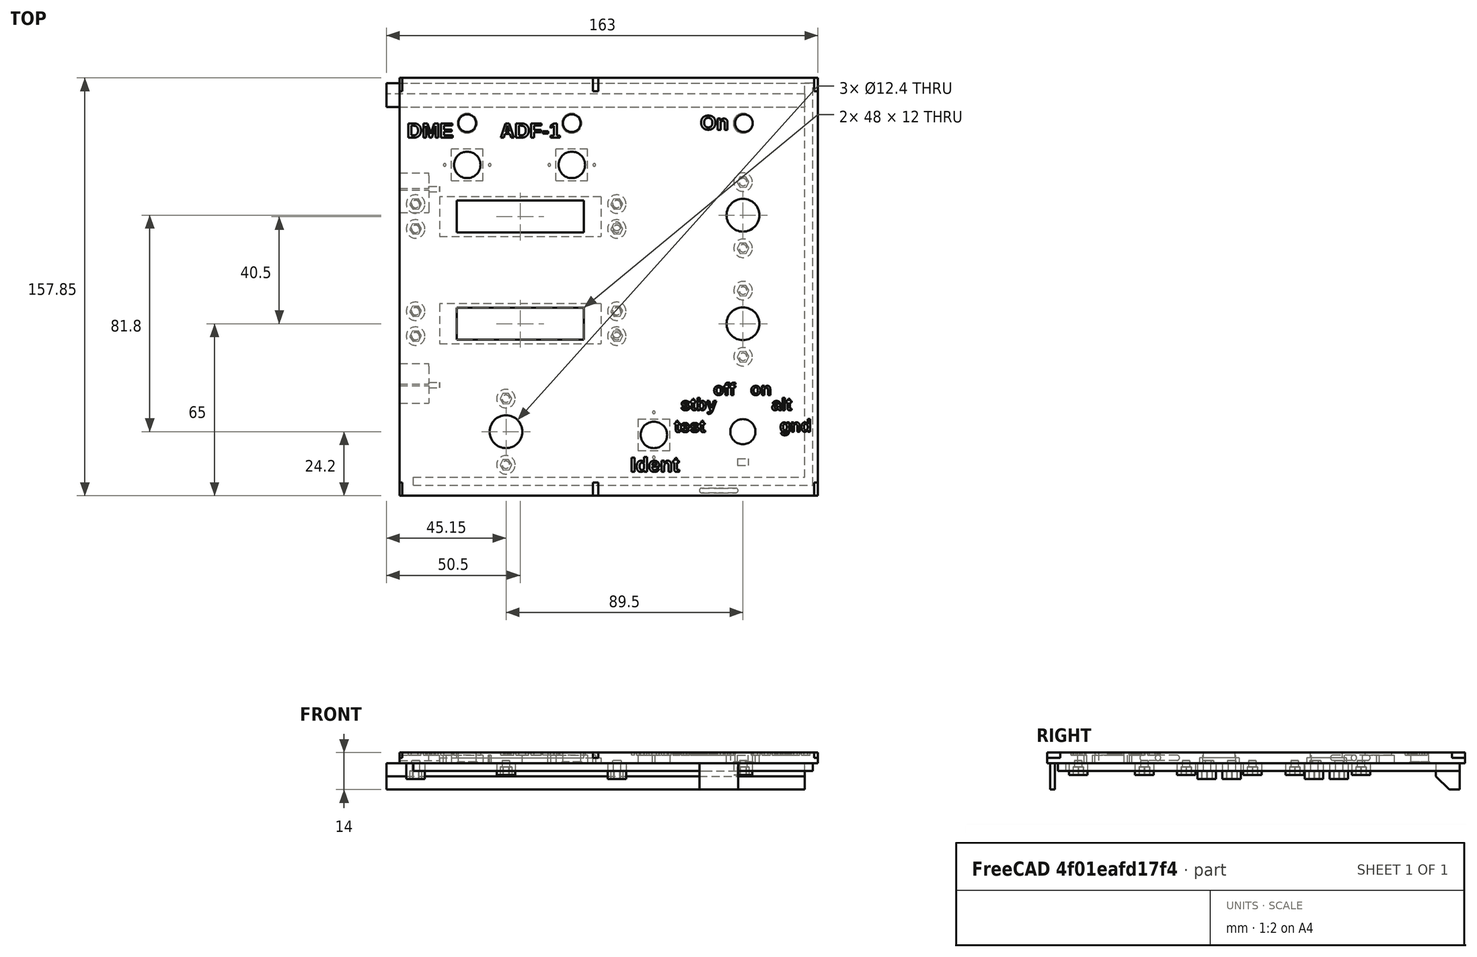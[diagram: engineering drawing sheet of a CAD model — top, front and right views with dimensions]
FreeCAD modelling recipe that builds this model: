
FCSTD DOCUMENT  (FreeCAD 0.17R13522 (Git))
Label: panel_frente_derecho
License: CreativeCommons Attribution-ShareAlike
LicenseURL: http://creativecommons.org/licenses/by-sa/4.0/
objects: Part::Feature×10, Part::Cut×10, Part::Box×3, Part::MultiFuse×2
note: 25 computed .brp shape members not serialized (recipe doc carries the construction recipe); baked Part::Feature solids carry a one-line shape summary decoded from their .brp

FEATURE [Part::Feature] Cut001001001002003001008002002033001001001001001001001002001001002001042002001  label="Cut001001001002003001008002002033001001001001001001001002001001002001042003"
  shape: bbox 163 x 157.9 x 19 mm, 920 faces (baked)
FEATURE [Part::Box] Box  label="apoyo_fleje_lateral"
  AttacherType = Attacher::AttachEngine3D
  Height = 2
  Length = 1.5
  Placement = pos=(129.5,-4,-105) rot=(0,0,1;0rad)
  Width = 5
FEATURE [Part::Feature] Box001  label="apoyo_fleje_lateral001"
  Placement = pos=(129.5,148.85,-105) rot=(0,0,1;0rad)
  shape: bbox 1.5 x 5 x 2 mm, 6 faces (baked)
FEATURE [Part::Feature] Box001001  label="apoyo_fleje_lateral002"
  Placement = pos=(286.5,148.85,-105) rot=(0,0,1;0rad)
  shape: bbox 1.5 x 5 x 2 mm, 6 faces (baked)
FEATURE [Part::Feature] Box001001001  label="apoyo_fleje_lateral003"
  Placement = pos=(286.5,-4,-105) rot=(0,0,1;0rad)
  shape: bbox 1.5 x 5 x 2 mm, 6 faces (baked)
FEATURE [Part::Cut] Cut
  Base = -> Cut001001001002003001008002002033001001001001001001001002001001002001042002001
  Refine = true
  Tool = -> Box001001001
FEATURE [Part::Cut] Cut001001001002003001008002002033001001001001001001001002001001002001042002002
  Base = -> Cut
  Refine = true
  Tool = -> Box001001
FEATURE [Part::Cut] Cut001001001002003001008002002033001001001001001001001002001001002001042002003
  Base = -> Cut001001001002003001008002002033001001001001001001001002001001002001042002002
  Refine = true
  Tool = -> Box
FEATURE [Part::Cut] Cut001001001002003001008002002033001001001001001001001002001001002001042002004
  Base = -> Cut001001001002003001008002002033001001001001001001001002001001002001042002003
  Refine = true
  Tool = -> Box001
FEATURE [Part::Box] Box001001002  label="Cube"
  AttacherType = Attacher::AttachEngine3D
  Height = 2
  Length = 2
  Placement = pos=(203,-4,-105) rot=(0,0,1;0rad)
  Width = 5
FEATURE [Part::Feature] Box001001002001  label="Cube001"
  Placement = pos=(203,148.85,-105) rot=(0,0,1;0rad)
  shape: bbox 2 x 5 x 2 mm, 6 faces (baked)
FEATURE [Part::Cut] Cut001001001002003001008002002033001001001001001001001002001001002001042002005
  Base = -> Cut001001001002003001008002002033001001001001001001001002001001002001042002004
  Refine = true
  Tool = -> Box001001002001
FEATURE [Part::Cut] Cut001001001002003001008002002033001001001001001001001002001001002001042002006
  Base = -> Cut001001001002003001008002002033001001001001001001001002001001002001042002005
  Refine = true
  Tool = -> Box001001002
FEATURE [Part::Feature] Body001  label="cortador_parea_encastres"
  Placement = pos=(141,45,-105) rot=(-0.57735,0.57735,0.57735;4.18879rad)
  shape: bbox 20 x 15 x 2 mm, 6 faces (baked)
FEATURE [Part::Cut] Cut001001001002003001008002002033001001001001001001001002001001002001042002007
  Base = -> Cut001001001002003001008002002033001001001001001001001002001001002001042002006
  Tool = -> Body001
FEATURE [Part::Feature] Body001001  label="cortador_parea_encastres001"
  Placement = pos=(141,117,-105) rot=(0.57735,-0.57735,-0.57735;2.0944rad)
  shape: bbox 20 x 15 x 2 mm, 6 faces (baked)
FEATURE [Part::Cut] Cut001001001002003001008002002033001001001001001001001002001001002001042002008
  Base = -> Cut001001001002003001008002002033001001001001001001001002001001002001042002007
  Tool = -> Body001001
FEATURE [Part::Feature] Body002  label="encastres001"
  Placement = pos=(244,-2,-126) rot=(0,0,1;0rad)
  shape: bbox 14.6 x 1.8 x 20 mm, 6 faces (baked)
FEATURE [Part::Box] Box001001002002  label="Cube002"
  AttacherType = Attacher::AttachEngine3D
  Height = 17
  Length = 13
  Placement = pos=(245,-14,-124) rot=(0,0,1;0rad)
  Width = 14
FEATURE [Part::Feature] Box001001002002001  label="Cube003"
  Placement = pos=(250,-10,-134) rot=(0,0,1;0rad)
  shape: bbox 13 x 14 x 17 mm, 6 faces (baked)
FEATURE [Part::Cut] Cut001001001002003001008002002033001001001001001001001002001001002001042002009
  Base = -> Cut001001001002003001008002002033001001001001001001001002001001002001042002008
  Tool = -> Box001001002002
FEATURE [Part::Feature] Box001001002002001001  label="Cube004"
  Placement = pos=(238,-10,-134) rot=(0,0,1;0rad)
  shape: bbox 13 x 14 x 17 mm, 6 faces (baked)
FEATURE [Part::MultiFuse] Fusion
  Shapes = -> [Box001001002002001001,Box001001002002001]
FEATURE [Part::Cut] Cut001001001002003001008002002033001001001001001001001002001001002001042002010
  Base = -> Body002
  Placement = pos=(0.1,0,0) rot=(0,0,1;0rad)
  Tool = -> Fusion
FEATURE [Part::MultiFuse] Fusion001  label="panel derecho"
  Shapes = -> [Cut001001001002003001008002002033001001001001001001001002001001002001042002010,Cut001001001002003001008002002033001001001001001001001002001001002001042002009]
